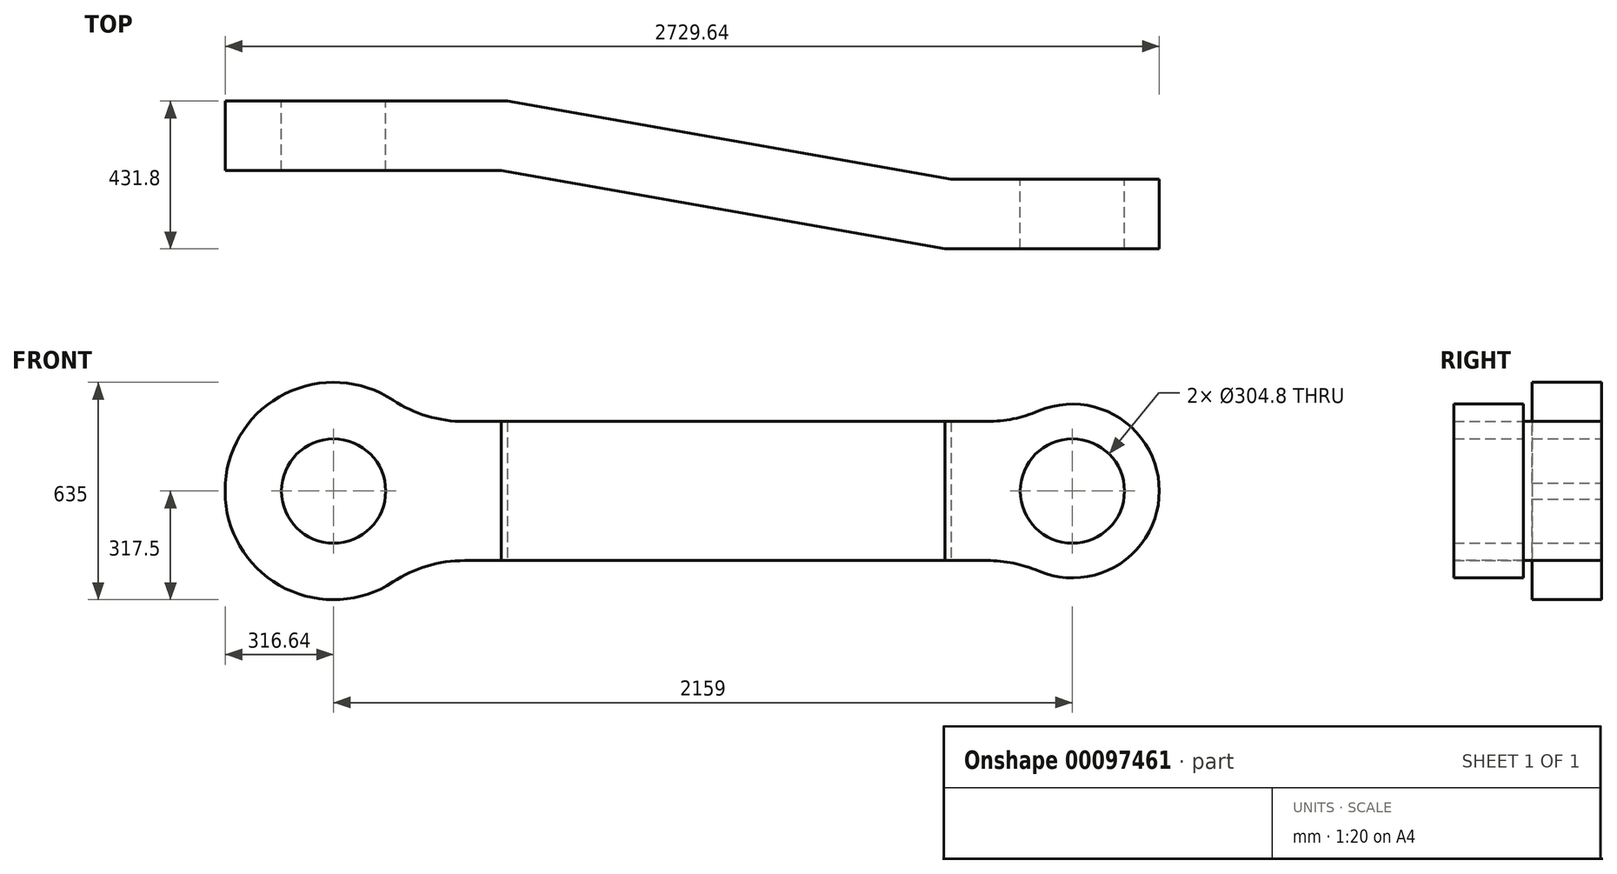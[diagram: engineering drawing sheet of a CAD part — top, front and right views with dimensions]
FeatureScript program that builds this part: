
annotation { "Feature Type Name" : "Feature", "Feature Type Description" : "" }
export const myFeature = defineFeature(function(context is Context, id is Id, definition is map)
    precondition{}
    {
        {
            var Q0;
            Q0=qCreatedBy(makeId("Front.planeOp"),FACE);
            var sketch = newSketch(context, id + "F0", { "sketchPlane" : qUnion([Q0])});
            skCircle(sketch, "E0", {"center": v(0, 0) * mm, "radius": 317.5 * mm});
            skCircle(sketch, "E1", {"center": v(2159, 0) * mm, "radius": 254 * mm});
            skLineSegment(sketch, "E2", {"start": v(0, 0) * mm, "end": v(2159, 0) * mm, "construction": true});
            skLineSegment(sketch, "E3", {"start": v(243.96, 203.2) * mm, "end": v(2006.6, 203.2) * mm});
            skLineSegment(sketch, "E4.MirrorCS", {"start": v(243.96, -203.2) * mm, "end": v(2006.6, -203.2) * mm});
            skCircle(sketch, "E5", {"center": v(0, 0) * mm, "radius": 152.4 * mm});
            skCircle(sketch, "E6", {"center": v(2159, 0) * mm, "radius": 152.4 * mm});
            skSolve(sketch);
        }
        {
            var Q0;
            Q0 = qSketchRegion(id + "F0", true);
            extrude(context, id + "F1", {"entities" : qUnion([Q0]), "depth" : 635 * mm});
        }
        {
            var Q0;
            Q0=qCreatedBy(makeId("Top.planeOp"),FACE);
            var sketch = newSketch(context, id + "F2", { "sketchPlane" : qUnion([Q0])});
            skLineSegment(sketch, "E7", {"start": v(-316.64, 0) * mm, "end": v(508, 0) * mm});
            skLineSegment(sketch, "E8", {"start": v(508, 0) * mm, "end": v(1804.46, -228.6) * mm});
            skLineSegment(sketch, "E9", {"start": v(1804.46, -228.6) * mm, "end": v(2415.6, -228.6) * mm});
            skLineSegment(sketch, "E10.0", {"start": v(1786.68, -431.8) * mm, "end": v(2415.6, -431.8) * mm});
            skLineSegment(sketch, "E10.1", {"start": v(490.22, -203.2) * mm, "end": v(1786.68, -431.8) * mm});
            skLineSegment(sketch, "E10.2", {"start": v(-316.64, -203.2) * mm, "end": v(490.22, -203.2) * mm});
            skLineSegment(sketch, "E11", {"start": v(2415.6, -228.6) * mm, "end": v(2415.6, -431.8) * mm});
            skLineSegment(sketch, "E12", {"start": v(-316.64, 0) * mm, "end": v(-316.64, -203.2) * mm});
            skLineSegment(sketch, "E13", {"start": v(2413, 0) * mm, "end": v(2413, -635) * mm});
            skLineSegment(sketch, "E14.0.0", {"start": v(243.96, 0) * mm, "end": v(-317.5, 0) * mm});
            skLineSegment(sketch, "E14.0.1", {"start": v(243.96, 0) * mm, "end": v(243.96, -635) * mm});
            skLineSegment(sketch, "E14.0.2", {"start": v(-317.5, -635) * mm, "end": v(243.96, -635) * mm});
            skLineSegment(sketch, "E14.0.3", {"start": v(243.96, -635) * mm, "end": v(243.96, 0) * mm});
            skSolve(sketch);
        }
        {
            var Q0;
            Q0 = qSketchRegion(id + "F2", true);
            extrude(context, id + "F3", {"entities" : qUnion([Q0]), "operationType" : NewBodyOperationType.INTERSECT, "endBound" : BoundingType.SYMMETRIC, "depth" : 635 * mm});
        }
        {
            var Q0;
            Q0=makeQuery(id+"F3.boolean.opBoolean","COPY",EDGE,{"derivedFrom":makeQuery(id+"F3.boolean.toolComplement.opBoolean","COPY",EDGE,{"derivedFrom":makeQuery(id+"F3.opExtrude","SWEPT_EDGE",EDGE,{"disambiguationData":[OSD([sQuery(id+"F2.wireOp",EDGE,"E7"),sQuery(id+"F2.wireOp",EDGE,"E8")])]})})});
            var Q1;
            Q1=makeQuery(id+"F3.boolean.opBoolean","COPY",EDGE,{"derivedFrom":makeQuery(id+"F3.boolean.toolComplement.opBoolean","COPY",EDGE,{"derivedFrom":makeQuery(id+"F3.opExtrude","SWEPT_EDGE",EDGE,{"disambiguationData":[OSD([sQuery(id+"F2.wireOp",EDGE,"E8"),sQuery(id+"F2.wireOp",EDGE,"E9")])]})})});
            var Q2;
            Q2=makeQuery(id+"F3.boolean.opBoolean","COPY",EDGE,{"derivedFrom":makeQuery(id+"F3.boolean.toolComplement.opBoolean","COPY",EDGE,{"derivedFrom":makeQuery(id+"F3.opExtrude","SWEPT_EDGE",EDGE,{"disambiguationData":[OSD([sQuery(id+"F2.wireOp",EDGE,"E10.1"),sQuery(id+"F2.wireOp",EDGE,"E10.2")])]})})});
            var Q3;
            Q3=makeQuery(id+"F3.boolean.opBoolean","COPY",EDGE,{"derivedFrom":makeQuery(id+"F3.boolean.toolComplement.opBoolean","COPY",EDGE,{"derivedFrom":makeQuery(id+"F3.opExtrude","SWEPT_EDGE",EDGE,{"disambiguationData":[OSD([sQuery(id+"F2.wireOp",EDGE,"E10.0"),sQuery(id+"F2.wireOp",EDGE,"E10.1")])]})})});
            var Q4;
            Q4=makeQuery(id+"F1.opExtrude","SWEPT_EDGE",EDGE,{"disambiguationData":[OSD([sQuery(id+"F0.wireOp",EDGE,"E0"),sQuery(id+"F0.wireOp",EDGE,"E3")])]});
            var Q5;
            Q5=makeQuery(id+"F1.opExtrude","SWEPT_EDGE",EDGE,{"disambiguationData":[OSD([sQuery(id+"F0.wireOp",EDGE,"E1"),sQuery(id+"F0.wireOp",EDGE,"E3")])]});
            var Q6;
            Q6=makeQuery(id+"F1.opExtrude","SWEPT_EDGE",EDGE,{"disambiguationData":[OSD([sQuery(id+"F0.wireOp",EDGE,"E1"),sQuery(id+"F0.wireOp",EDGE,"E4.MirrorCS")])]});
            var Q7;
            Q7=makeQuery(id+"F1.opExtrude","SWEPT_EDGE",EDGE,{"disambiguationData":[OSD([sQuery(id+"F0.wireOp",EDGE,"E0"),sQuery(id+"F0.wireOp",EDGE,"E4.MirrorCS")])]});
            fillet(context, id + "F4", {"entities" : qUnion([Q0, Q1, Q2, Q3, Q4, Q5, Q6, Q7]), "radius" : 381 * mm, "tangentPropagation" : true, "allowEdgeOverflow" : false});
        }
    });
